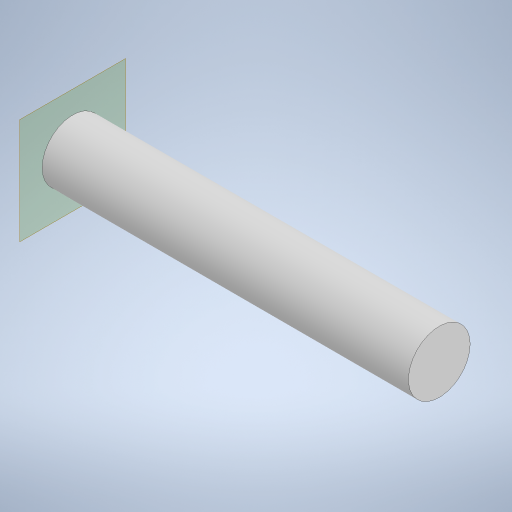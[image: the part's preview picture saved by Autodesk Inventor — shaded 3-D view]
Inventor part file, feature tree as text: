
AUTODESK INVENTOR PART (.ipt)
format: ipt  version: 2023 (Build 270158000, 158)  size: 238,080 bytes
history: native  units: in
note: dims shown in document units (in); Inventor stores cm internally (conversion verified against a paired STEP export)
features: plane x1, extrude x1, draft x1, sketch x1
ambient origin geometry x8: Origin, YZ Plane, XZ Plane, XY Plane, X Axis, Y Axis, Z Axis, Center Point
bodies: Body1 (feature_tree)
feature tree (4):
  plane  "Work Plane1"
  extrude  "Extrusion2"  Depth=0.0003in
  draft  "FaceDraft1"
  sketch  "Sketch3"  dims[d14=3.0in d15=0.0in d16=0.0003in]
